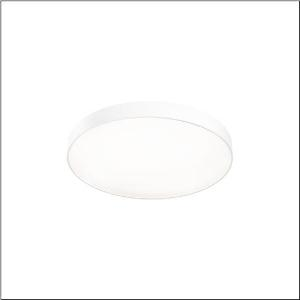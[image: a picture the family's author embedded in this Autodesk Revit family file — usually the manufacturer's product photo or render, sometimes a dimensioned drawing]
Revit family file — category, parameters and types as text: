
# Revit family: round_21_m_51mr36gd0321w
name_source: partatom
category: Lighting Fixtures
units: mm (PartAtom-declared; Revit-internal decimal feet)

## family parameters
Cut with Voids When Loaded = No
Host = Face
Light Source = No
Part Type = Normal
Room Calculation Point = No
Round Connector Dimension = Use Diameter
Shared = No

## types (1)
- Round 21 M (1 x LED, 6840 lm, 54.5 W, 3000K)
    Apparent Load = 55 VA
    CIE Flux Codes = 49 80 96 85 100
    Color Rendering = 80
    Color Temperature = 3000K
    Default Elevation = 1800 mm
    Description = Round 21 M, wall and ceiling luminaire, primary optical cover: cover, of PMMA, opal, light emission: direct/indirect distribution, primary light characteristic: symmetric, installation type: suspended mounting, surface-mounted, LED, rated luminous flux: 6.790lm, luminous efficacy: 124lm/W, light colour: 830, colour temperature: 3000K, with terminal, 5-pole, mains connection: 230V, AC, 50/60Hz, rated input power: 55W, housing, of aluminium, coated, white, diameter: 600mm, height: 62mm, protection rating (complete): IP40, insulation class (complete): insulation class I (protective earthing), certification: CE, impact resistance: IK04, permissible operating ambient temperature: -10..+35°C, packaging unit: 1 piece
    Height = 87 mm
    Lamp = 1 x LED
    Lamp Light Flux = 6840 lm
    Lamp Power = 54.5 W
    Lamp count = 1
    Length = 600 mm
    Luminous efficacy = 126 lm/W
    Manufacturer = Siteco
    ModVariant = No
    Model = 51MR36GD0321W
    Mounting Place = Ceiling
    Mounting Type = Surface mounted
    Number of Poles = 1
    OnlyDefault = Yes
    Power Factor = 1
    Product Name = Round 21 M
    Product group = wall and ceiling luminaire
    ProductGroupID = 301
    Protection Class = Protection class I
    Protection Degree = IP 40
    RLX_Detail_Level = 1
    RLX_Emergency_Light_Flux = 0 lm
    RLX_Emergency_Type = 0
    RLX_Emergency_Type_DB = No
    RlxData = <blob elided: 12097 chars, md5=5d31522b>
    Socket = socket
    Standby Power = 0 W
    System Light Flux = 6840 lm
    System Power = 55 W
    Type Comments = Product without accessories
    Type Image = l_1258330.jpg
    URL = http://relux.com
    VarID = ---
    Voltage = 0 V
    Weight = 0.00 kg
    Width = 0 mm  [stored 0 ft]

note: [stored X ft] marks values corroborated as IEEE doubles in the binary element streams (Revit-internal decimal feet)

## geometry (parser evidence)
native form markers: Sweep x12
no freeform markers — native parametric forms only
